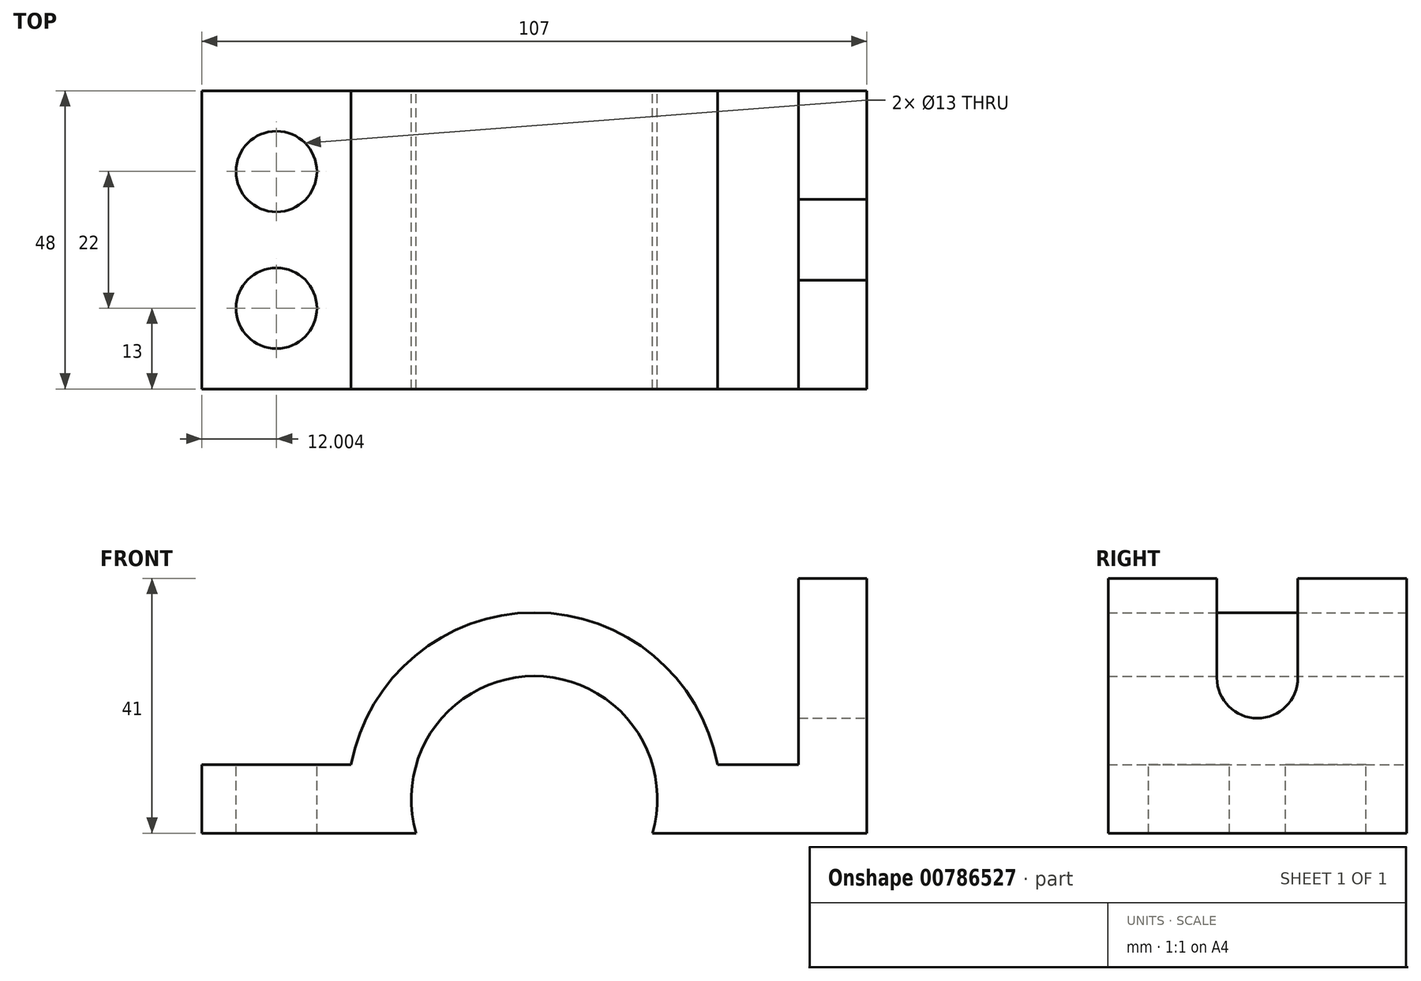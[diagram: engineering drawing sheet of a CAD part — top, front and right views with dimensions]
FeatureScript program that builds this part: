
annotation { "Feature Type Name" : "Feature", "Feature Type Description" : "" }
export const myFeature = defineFeature(function(context is Context, id is Id, definition is map)
    precondition{}
    {
        {
            var Q0;
            Q0=qCreatedBy(makeId("Front.planeOp"),FACE);
            var sketch = newSketch(context, id + "F0", { "sketchPlane" : qUnion([Q0])});
            skArc(sketch, "E0", {"start": v(19, -5.5) * mm, "mid": v(0, 19.78) * mm, "end": v(-19, -5.5) * mm});
            skArc(sketch, "E1", {"start": v(29.5, 5.5) * mm, "mid": v(0, 30) * mm, "end": v(-29.5, 5.5) * mm});
            skLineSegment(sketch, "E2.bottom", {"start": v(53.5, -5.5) * mm, "end": v(19, -5.5) * mm});
            skLineSegment(sketch, "E2.top", {"start": v(42.5, 5.5) * mm, "end": v(29.5, 5.5) * mm});
            skLineSegment(sketch, "E2.left", {"start": v(53.5, -5.5) * mm, "end": v(53.5, 5.5) * mm});
            skLineSegment(sketch, "E2.right", {"start": v(-53.5, -5.5) * mm, "end": v(-53.5, 5.5) * mm});
            skLineSegment(sketch, "E3.trimOffspring", {"start": v(-19, -5.5) * mm, "end": v(-53.5, -5.5) * mm});
            skLineSegment(sketch, "E4.trimOffspring", {"start": v(-29.5, 5.5) * mm, "end": v(-53.5, 5.5) * mm});
            skLineSegment(sketch, "E5.top", {"start": v(53.5, 35.5) * mm, "end": v(42.5, 35.5) * mm});
            skLineSegment(sketch, "E5.left", {"start": v(53.5, 5.5) * mm, "end": v(53.5, 35.5) * mm});
            skLineSegment(sketch, "E5.right", {"start": v(42.5, 5.5) * mm, "end": v(42.5, 35.5) * mm});
            skSolve(sketch);
        }
        {
            var Q0;
            Q0 = qSketchRegion(id + "F0", true);
            extrude(context, id + "F1", {"entities" : qUnion([Q0]), "depth" : 48 * mm, "offsetDistance" : 25 * mm});
        }
        {
            var Q0;
            Q0=makeQuery(id+"F1.opExtrude","SWEPT_FACE",FACE,{"disambiguationData":[OSD([sQuery(id+"F0.wireOp",EDGE,"E4.trimOffspring")])]});
            var sketch = newSketch(context, id + "F2", { "sketchPlane" : qUnion([Q0])});
            skLineSegment(sketch, "E6", {"start": v(-53.5, -24) * mm, "end": v(-29.5, -24) * mm, "construction": true});
            skCircle(sketch, "E7", {"center": v(-41.5, -35) * mm, "radius": 6.5 * mm});
            skPoint(sketch, "E7.centerSnap0", {"position": v(-41.5, -24) * mm});
            skCircle(sketch, "E8.MirrorC", {"center": v(-41.5, -13) * mm, "radius": 6.5 * mm});
            skSolve(sketch);
        }
        {
            var Q0;
            Q0 = qSketchRegion(id + "F2", true);
            extrude(context, id + "F3", {"entities" : qUnion([Q0]), "operationType" : NewBodyOperationType.REMOVE, "oppositeDirection" : true, "depth" : 11 * mm, "offsetDistance" : 25 * mm});
        }
        {
            var Q0;
            Q0=makeQuery(id+"F1.opExtrude","SWEPT_FACE",FACE,{"disambiguationData":[OSD([sQuery(id+"F0.wireOp",EDGE,"E2.left"),sQuery(id+"F0.wireOp",EDGE,"E5.left")])]});
            var sketch = newSketch(context, id + "F4", { "sketchPlane" : qUnion([Q0])});
            skSolve(sketch);
        }
        {
            var Q0;
            {var subQ0=sQuery(id+"F0.wireOp",EDGE,"E2.left");Q0=makeQuery(id+"F4.imprint","IMPRINT",FACE,{"disambiguationData":[TD([[makeQuery(id+"F4.imprint","IMPRINT",EDGE,{"derivedFrom":makeQuery(id+"F1.opExtrude","SWEPT_EDGE",EDGE,{"disambiguationData":[OSD([sQuery(id+"F0.wireOp",EDGE,"E2.bottom"),subQ0])]})}),1.0]])]});}
            var sketch = newSketch(context, id + "F5", { "sketchPlane" : qUnion([Q0])});
            skLineSegment(sketch, "E9", {"start": v(0, -5.5) * mm, "end": v(-24, -5.5) * mm, "construction": true});
            skLineSegment(sketch, "E10", {"start": v(0, -5.5) * mm, "end": v(0, 19.5) * mm, "construction": true});
            skLineSegment(sketch, "E11", {"start": v(0, 19.5) * mm, "end": v(-48, 19.5) * mm, "construction": true});
            skLineSegment(sketch, "E12", {"start": v(-24, -5.5) * mm, "end": v(-24, 35.5) * mm, "construction": true});
            skArc(sketch, "E13", {"start": v(-30.5, 19.5) * mm, "mid": v(-24, 13) * mm, "end": v(-17.5, 19.5) * mm});
            skLineSegment(sketch, "E14.bottom", {"start": v(-17.5, 19.5) * mm, "end": v(-30.5, 19.5) * mm});
            skLineSegment(sketch, "E14.top", {"start": v(-17.5, 35.5) * mm, "end": v(-30.5, 35.5) * mm});
            skLineSegment(sketch, "E14.left", {"start": v(-17.5, 19.5) * mm, "end": v(-17.5, 35.5) * mm});
            skLineSegment(sketch, "E14.right", {"start": v(-30.5, 19.5) * mm, "end": v(-30.5, 35.5) * mm});
            skSolve(sketch);
        }
        {
            var Q0;
            Q0 = qSketchRegion(id + "F5", true);
            extrude(context, id + "F6", {"entities" : qUnion([Q0]), "operationType" : NewBodyOperationType.REMOVE, "oppositeDirection" : true, "depth" : 12 * mm, "offsetDistance" : 25 * mm});
        }
    });
